# Revit family: Sanitary_Wash-basins_hansgrohe_22438CHN-LakeShore-Q-Wash-bowl-500-380-w_NEW
name_source: partatom
category: Plumbing Fixtures
units: mm (PartAtom-declared; Revit-internal decimal feet)

## family parameters
Cut with Voids When Loaded = Yes
Host = Face
OmniClass Number = 23.31.13.00
OmniClass Title = Sinks
Part Type = Normal
Room Calculation Point = No
Round Connector Dimension = Use Diameter
Shared = No

## types (1)
- 007 White
    Connector Description = Water Outlet 46 mm
    Default Elevation = 1219 mm
    Description = LakeShore Q Wash bowl 500/380 without tap hole and overflow, SmartClean
    Diameter = 46 mm  [stored 0.150919 ft]
    Manufacturer = Hansgrohe
    Material 1 = Hansgrohe - Ceramic - 007 White
    Model = 22438CHN
    Product Guid = 92b1b15f-b2f6-4d45-99bd-ce34061c309f
    Product Page URL = https://pro.hansgrohe.com
    Product data url = https://bimobject.com
    URL = https://www.hansgrohe.com
    Version = 1

note: [stored X ft] marks values corroborated as IEEE doubles in the binary element streams (Revit-internal decimal feet)

## geometry (parser evidence)
native form markers: Sweep x3
no freeform markers — native parametric forms only
